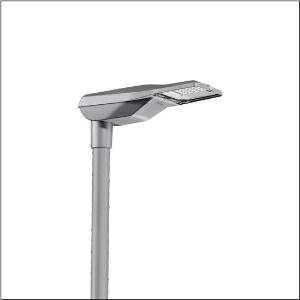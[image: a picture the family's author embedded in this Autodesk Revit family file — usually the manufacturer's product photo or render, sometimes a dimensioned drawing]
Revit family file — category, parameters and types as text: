
# Revit family: streetlight_sl_21_micro___st1_0a_5xe5d43a08cb_bbe5
name_source: partatom
category: Lighting Fixtures
units: mm (PartAtom-declared; Revit-internal decimal feet)

## family parameters
Cut with Voids When Loaded = No
Host = Face
Light Source = No
Part Type = Normal
Room Calculation Point = No
Round Connector Dimension = Use Diameter
Shared = No

## types (1)
- --- (1 x LED, 2380 lm, 15.8 W, 4000K)
    Apparent Load = 16 VA
    CIE Flux Codes = 37 72 97 100 100
    Color Rendering = 70
    Color Temperature = 4000K
    Default Elevation = 1800 mm
    Description = Streetlight SL 21 micro, mast luminaire, primary light control with lens, of PMMA, primary optical cover: cover, of toughened safety glass, transparent, light distribution: ST1.0a, light emission: direct distribution, primary light characteristic: asymmetric, installation type: side-entry, post-top, LED, 3G 1.5mm², High Power LED, rated luminous flux: 2.380lm, luminous efficacy: 151lm/W, light colour: 740, colour temperature: 4000K, control: flexible luminous flux parameterisation, time-dependent luminous flux control, constant luminous flux control, overheat protection, mains connection: 230..240V, AC, 50/60Hz, connection cable pre-assembled, cable length: 5,5m, wiring characteristics: H07RN-F, start of lifetime: 16W, end of service life: 16W, reduction: 9W, luminaire housing, of diecast aluminium, powder-coated, Siteco® metallic grey (DB 702S), corrosivity category C5 mid according to DIN EN ISO 12944, please order mast flange separately, inclination adjustable: 0°, 5°, 10°, 15°, sealing non-destructively replaceable, multi-level sealing system, length: 528mm, width: 235mm, height: 110mm, mast flange for spigot size: 42mm (side-entry): 5XC10008XM4, 60/48mm (side-entry/post-top): 5XC10108XM2, 76/60mm (side-entry/post-top): 5XC10108XM1, protection rating (complete): IP66, insulation class (complete): insulation class II (safety insulation), certification: CE, ENEC, ENEC+, VDE, impact resistance: IK09, permissible operating ambient temperature for outdoor applications: -40..+50°C, standard-compliant lighting for roads and squares, packaging unit: 1 piece

Light Distribution: ST1.0a
    Height = 110 mm
    Lamp = 1 x LED
    Lamp Light Flux = 2380 lm
    Lamp Power = 15.8 W
    Lamp count = 1
    Length = 528 mm
    Luminous efficacy = 151 lm/W
    Manufacturer = Siteco
    ModVariant = No
    Model = 5XE5D43A08CB
    Number of Poles = 1
    OnlyDefault = Yes
    Power Factor = 1
    Product Name = Streetlight SL 21 micro | ST1.0a
    Product group = mast luminaire | pylon top
    ProductGroupID = 6100
    Protection Class = Protection class II
    Protection Degree = IP 66
    RLX_Detail_Level = 1
    RLX_Emergency_Light_Flux = 0 lm
    RLX_Emergency_Type = 0
    RLX_Emergency_Type_DB = No
    RlxData = <blob elided: 97705 chars, md5=911761df>
    Socket = socket
    Standby Power = 0 W
    System Light Flux = 2380 lm
    System Power = 16 W
    Type Comments = factory setting: luminous flux: 100 % | Output Level: 100 % | 300 mA
    Type Image = l_1006881.jpg
    URL = http://relux.com
    VarID = @adj_105757
    Voltage = 0 V
    Weight = 0.00 kg
    Width = 235 mm

## geometry (parser evidence)
native form markers: Blend x4, Sweep x10
no freeform markers — native parametric forms only
